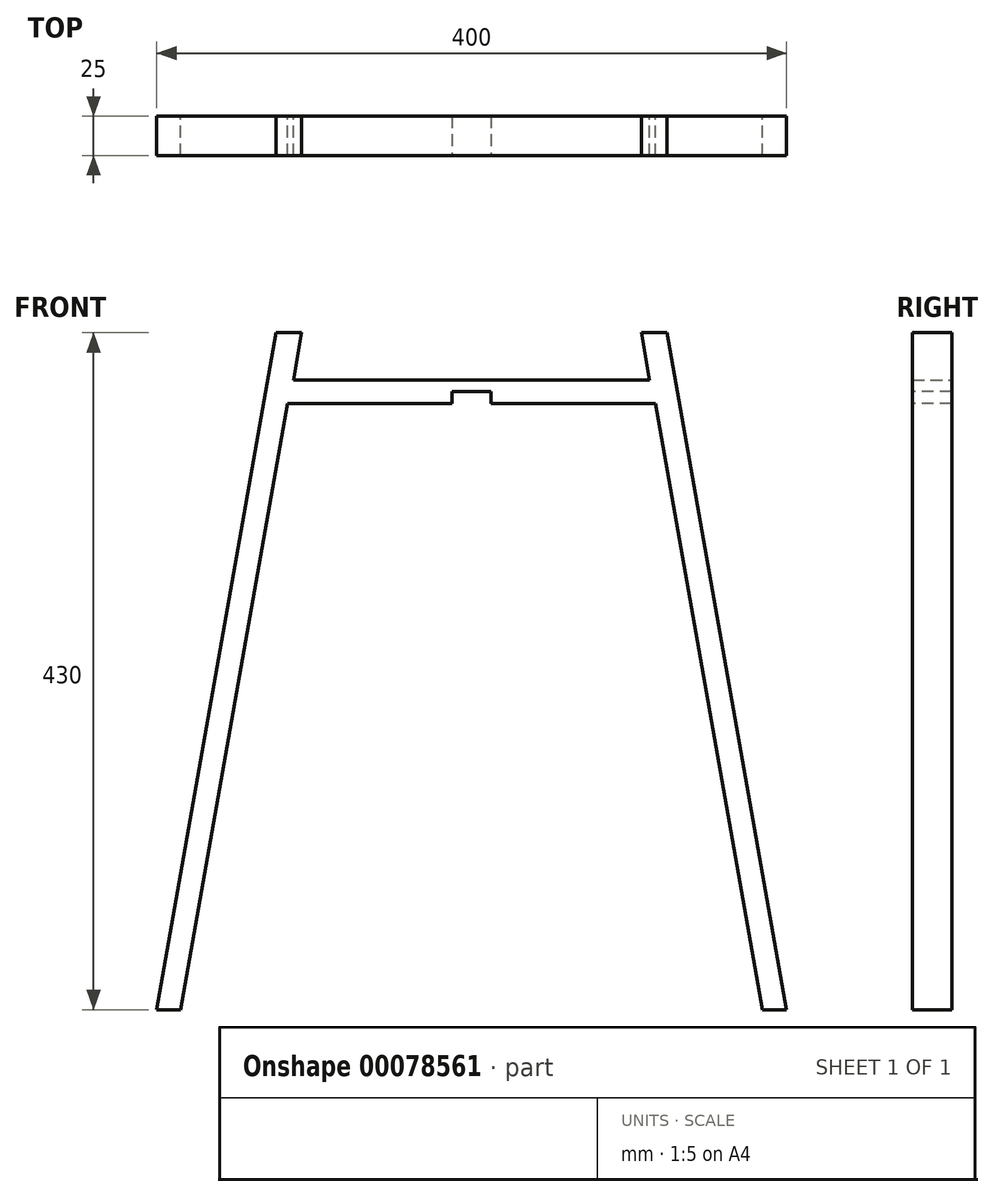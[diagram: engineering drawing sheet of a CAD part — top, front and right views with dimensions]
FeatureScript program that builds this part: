
annotation { "Feature Type Name" : "Feature", "Feature Type Description" : "" }
export const myFeature = defineFeature(function(context is Context, id is Id, definition is map)
    precondition{}
    {
        {
            var Q0;
            Q0=qCreatedBy(makeId("Front.planeOp"),FACE);
            var sketch = newSketch(context, id + "F0", { "sketchPlane" : qUnion([Q0])});
            skLineSegment(sketch, "E0", {"start": v(0, 385) * mm, "end": v(-116.88, 385) * mm});
            skLineSegment(sketch, "E1", {"start": v(-116.88, 385) * mm, "end": v(-184.77, 0) * mm});
            skLineSegment(sketch, "E2", {"start": v(-184.77, 0) * mm, "end": v(-200, 0) * mm});
            skLineSegment(sketch, "E3", {"start": v(-200, 0) * mm, "end": v(-124.18, 430) * mm});
            skLineSegment(sketch, "E4", {"start": v(-124.18, 430) * mm, "end": v(-107.82, 430) * mm});
            skLineSegment(sketch, "E5", {"start": v(-107.82, 430) * mm, "end": v(-113.11, 400) * mm});
            skLineSegment(sketch, "E6", {"start": v(-113.11, 400) * mm, "end": v(0, 400) * mm});
            skLineSegment(sketch, "E7", {"start": v(0, 400) * mm, "end": v(0, 385) * mm});
            skLineSegment(sketch, "E8.MirrorCS", {"start": v(107.82, 430) * mm, "end": v(113.11, 400) * mm});
            skLineSegment(sketch, "E9.MirrorCS", {"start": v(124.18, 430) * mm, "end": v(107.82, 430) * mm});
            skLineSegment(sketch, "E10.MirrorCS", {"start": v(184.77, 0) * mm, "end": v(200, 0) * mm});
            skLineSegment(sketch, "E11.MirrorCS", {"start": v(116.88, 385) * mm, "end": v(184.77, 0) * mm});
            skLineSegment(sketch, "E12.MirrorCS", {"start": v(113.11, 400) * mm, "end": v(0, 400) * mm});
            skLineSegment(sketch, "E13.MirrorCS", {"start": v(200, 0) * mm, "end": v(124.18, 430) * mm});
            skLineSegment(sketch, "E14.MirrorCS", {"start": v(0, 385) * mm, "end": v(116.88, 385) * mm});
            skSolve(sketch);
        }
        {
            var Q0;
            Q0=qSketchRegion(id+"F0",true);
            extrude(context, id + "F1", {"entities" : qUnion([Q0]), "endBound" : BoundingType.SYMMETRIC, "depth" : 25 * mm});
        }
        {
            var Q0;
            Q0=qCreatedBy(makeId("Front.planeOp"),FACE);
            var sketch = newSketch(context, id + "F2", { "sketchPlane" : qUnion([Q0])});
            skLineSegment(sketch, "E15", {"start": v(0, -22.46) * mm, "end": v(0, 481.86) * mm, "construction": true});
            skLineSegment(sketch, "E16.bottom", {"start": v(12.5, 392.5) * mm, "end": v(-12.5, 392.5) * mm});
            skLineSegment(sketch, "E16.top", {"start": v(12.5, 385) * mm, "end": v(-12.5, 385) * mm});
            skLineSegment(sketch, "E16.left", {"start": v(12.5, 392.5) * mm, "end": v(12.5, 385) * mm});
            skLineSegment(sketch, "E16.right", {"start": v(-12.5, 392.5) * mm, "end": v(-12.5, 385) * mm});
            skSolve(sketch);
        }
        {
            var Q0;
            Q0=qSketchRegion(id+"F2",true);
            extrude(context, id + "F3", {"entities" : qUnion([Q0]), "operationType" : NewBodyOperationType.REMOVE, "endBound" : BoundingType.SYMMETRIC, "oppositeDirection" : true, "depth" : 25 * mm});
        }
    });
